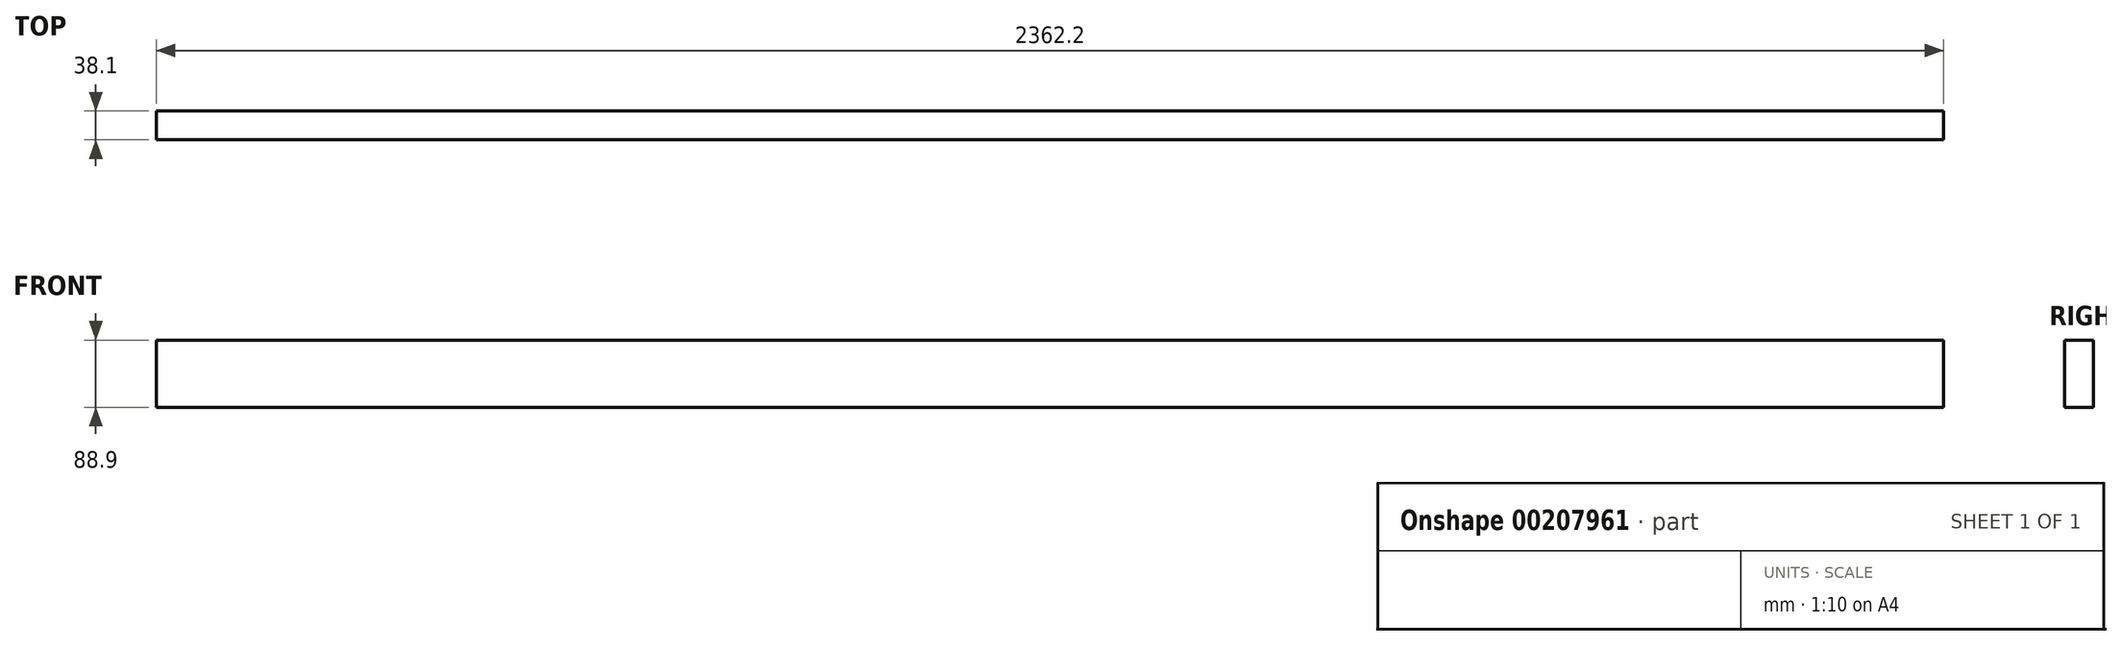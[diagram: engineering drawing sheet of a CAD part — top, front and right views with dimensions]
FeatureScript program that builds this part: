
annotation { "Feature Type Name" : "Feature", "Feature Type Description" : "" }
export const myFeature = defineFeature(function(context is Context, id is Id, definition is map)
    precondition{}
    {
        {
            var Q0;
            Q0=qCreatedBy(makeId("Right.planeOp"),FACE);
            var sketch = newSketch(context, id + "F0", { "sketchPlane" : qUnion([Q0])});
            skLineSegment(sketch, "E0.bottom", {"start": v(0, 0) * mm, "end": v(38.1, 0) * mm});
            skLineSegment(sketch, "E0.top", {"start": v(0, 88.9) * mm, "end": v(38.1, 88.9) * mm});
            skLineSegment(sketch, "E0.left", {"start": v(0, 0) * mm, "end": v(0, 88.9) * mm});
            skLineSegment(sketch, "E0.right", {"start": v(38.1, 0) * mm, "end": v(38.1, 88.9) * mm});
            skSolve(sketch);
        }
        {
            var Q0;
            Q0 = qSketchRegion(id + "F0", true);
            extrude(context, id + "F1", {"entities" : qUnion([Q0]), "depth" : 2362.2 * mm});
        }
    });
